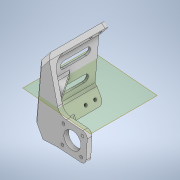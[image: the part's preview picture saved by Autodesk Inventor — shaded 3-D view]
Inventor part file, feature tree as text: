
AUTODESK INVENTOR PART (.ipt)
format: ipt  version: 2020 (Build 240168000, 168)  size: 387,584 bytes
history: native  units: mm
features: sketch x9, projected_geometry x9, reference x8, extrude x7, fillet x6, other x4, hole x2, plane x2, shell x2, chamfer x1
ambient origin geometry x8: Origin, YZ Plane, XZ Plane, XY Plane, X Axis, Y Axis, Z Axis, Center Point
bodies: Solid1 (feature_tree)
feature tree (50):
  extrude  "Extrusion1"  Depth=5.0mm
  hole  "Hole1"  [1 undecoded]
  hole  "Hole2"  [1 undecoded]
  extrude  "Extrusion2"  Depth=102.0mm
  sketch  "Sketch5"  dims[d13=3.0mm d14=6.0mm d15=4.0mm d16=2.0mm d17=90.0deg d18=8.0mm d19=20.594885mm d20=25.0mm d21=0.0mm]
  plane  "Work Plane1"
  extrude  "Extrusion3"  Depth=40.0mm
  extrude  "Extrusion4"  Depth=20.0mm
  plane  "Work Plane2"
  extrude  "Extrusion5"  Depth=8.0mm
  extrude  "Extrusion6"  Depth=8.0mm
  fillet  "Fillet1"  Radius=3.0mm
  fillet  "Fillet2"  Radius=3.0mm
  fillet  "Fillet3"  Radius=3.0mm
  fillet  "Fillet4"  Radius=18.0mm
  fillet  "Fillet5"  Radius=5.0mm
  fillet  "Fillet6"  Radius=30.0mm
  chamfer  "Chamfer1"  Distance=20.0mm
  extrude  "Extrusion7"  Depth=5.0mm TaperAngle=0.0deg
  sketch  "Sketch1"  dims[d0=5.0mm d1=5.0mm]
  reference  "Reference1"
  reference  "Reference2"
  sketch  "Sketch2"  dims[d2=5.0mm d3=5.0mm]
  reference  "Reference3"
  reference  "Reference4"
  sketch  "Sketch3"  dims[d4=25.0mm d5=0.0mm]
  reference  "Reference5"
  reference  "Reference6"
  sketch  "Sketch4"  dims[d6=3.0mm d7=6.0mm d8=4.0mm d9=2.0mm d10=90.0deg d11=8.0mm d12=20.594885mm]
  projected_geometry  "Projected Loop1"
  projected_geometry  "Projected Loop2"
  projected_geometry  "Projected Loop3"
  sketch  "Sketch6"  dims[d22=25.0mm d23=0.0mm d24=102.0mm]
  reference  "Reference7"
  reference  "Reference8"
  projected_geometry  "Projected Loop4"
  sketch  "Sketch7"  dims[d25=20.0mm d26=40.0mm]
  projected_geometry  "Projected Loop5"
  projected_geometry  "Projected Loop6"
  sketch  "Sketch8"  dims[d27=20.0mm d28=20.0mm]
  projected_geometry  "Projected Loop7"
  projected_geometry  "Projected Loop8"
  sketch  "Sketch9"  dims[d29=30.0mm d30=30.0mm d31=3.0mm d32=3.0mm d33=3.0mm d34=3.0mm d35=18.0mm d36=5.0mm d37=0.0mm d38=30.0mm d39=20.0mm d40=5.0mm d41=0.0mm d42=30.0mm d43=15.0mm d44=3.0mm d45=0.0mm d46=10.0mm d47=2.0mm d48=2.0mm d49=10.0mm d50=5.0mm d51=5.0mm d52=5.0mm d53=2.0mm d54=45.0deg d55=5.0mm d56=13.0mm d57=13.0mm d58=12.0mm d59=8.0mm d60=12.0mm d61=8.0mm d62=3.0mm d63=0.0mm]
  projected_geometry  "Projected Loop9"
  parser-record x1  (decoder bookkeeping rows leaked as tree rows — omitted from the tree; the rows remain in map.json)
  other  "reducer_2.iam"
  shell  "shell_2:3"  Thickness=30.0mm
  shell  "shell_2:4"  Thickness=15.0mm
  other  "bearing_8_16_5:3"
  other  "bearing_8_16_5:1"
note: 2 required parameter values undecoded (feature->parameter linkage not recoverable at this tier; creation-order binding heuristic only, values carry confidence <= 0.55)
note: 1 file-system path scrubbed to <path> (originals preserved in map.json)
